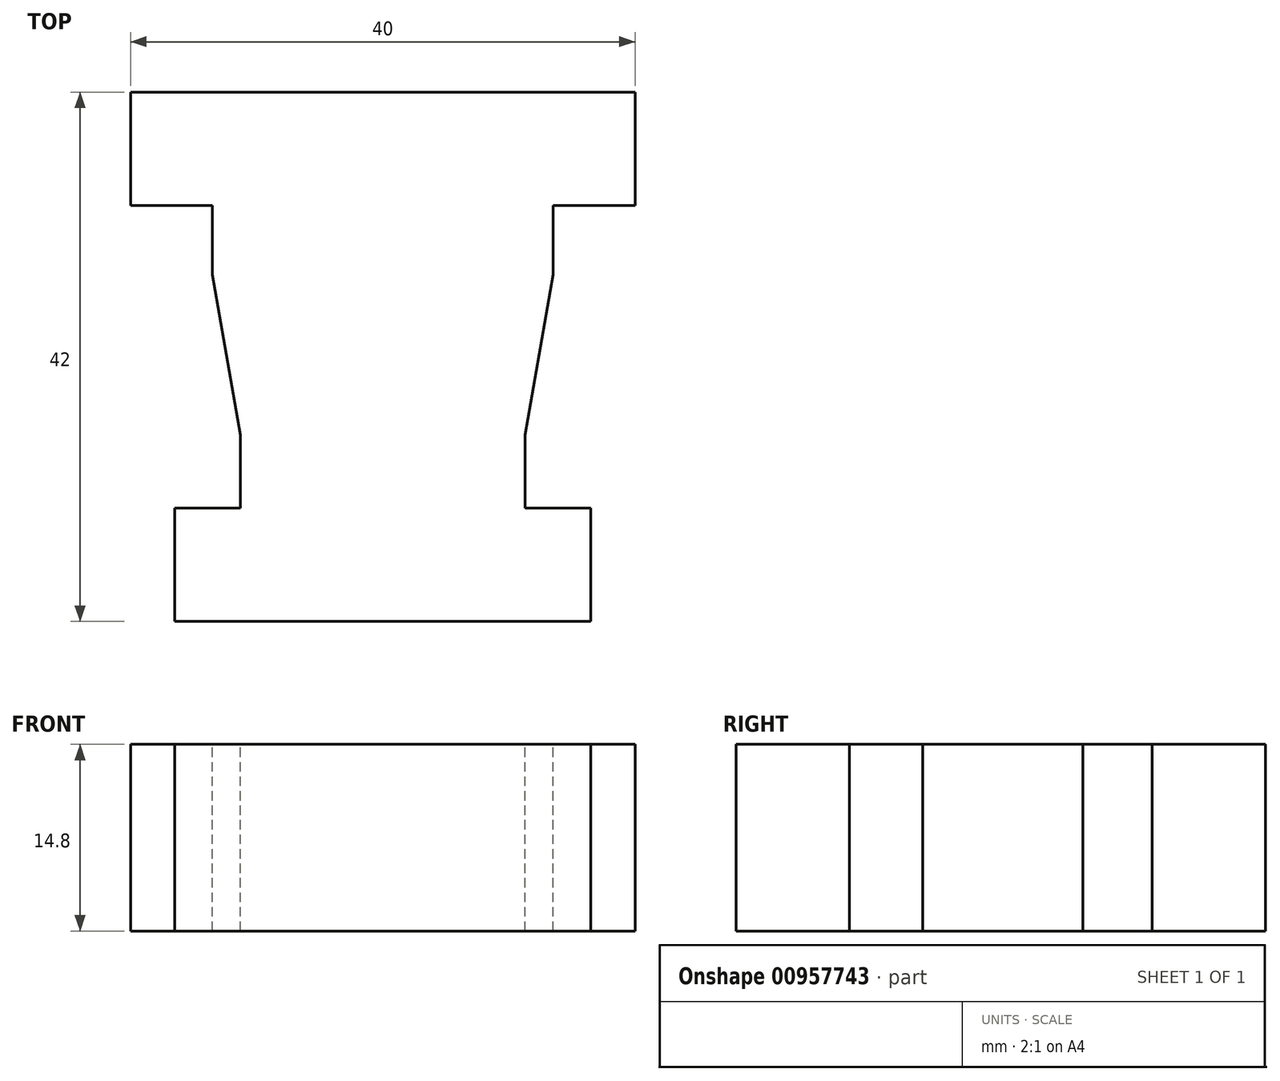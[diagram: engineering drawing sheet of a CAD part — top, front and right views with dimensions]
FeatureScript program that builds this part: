
annotation { "Feature Type Name" : "Feature", "Feature Type Description" : "" }
export const myFeature = defineFeature(function(context is Context, id is Id, definition is map)
    precondition{}
    {
        {
            var Q0;
            Q0=qCreatedBy(makeId("Top.planeOp"),FACE);
            var sketch = newSketch(context, id + "F0", { "sketchPlane" : qUnion([Q0])});
            skLineSegment(sketch, "E0.bottom", {"start": v(20, 21) * mm, "end": v(-20, 21) * mm});
            skLineSegment(sketch, "E0.top", {"start": v(20, -21) * mm, "end": v(-20, -21) * mm});
            skLineSegment(sketch, "E0.left", {"start": v(20, 21) * mm, "end": v(20, -21) * mm});
            skLineSegment(sketch, "E0.right", {"start": v(-20, 21) * mm, "end": v(-20, -21) * mm});
            skPoint(sketch, "E0.middle", {"position": v(0, 0) * mm});
            skSolve(sketch);
        }
        {
            var Q0;
            Q0=makeQuery(id+"F0.imprint","IMPRINT",FACE,{"disambiguationData":[TD([[makeQuery(id+"F0.imprint","IMPRINT",EDGE,{"derivedFrom":sQuery(id+"F0.wireOp",EDGE,"E0.bottom")}),1.0]])]});
            extrude(context, id + "F1", {"entities" : qUnion([Q0]), "depth" : 14.8 * mm, "offsetDistance" : 25 * mm});
        }
        {
            var Q0;
            Q0=makeQuery(id+"F1.opExtrude","CAP_FACE",FACE,{"disambiguationData":[OSD([sQuery(id+"F0.wireOp",EDGE,"E0.bottom"),sQuery(id+"F0.wireOp",EDGE,"E0.top"),sQuery(id+"F0.wireOp",EDGE,"E0.left"),sQuery(id+"F0.wireOp",EDGE,"E0.right")])],"isStart":false});
            var sketch = newSketch(context, id + "F2", { "sketchPlane" : qUnion([Q0])});
            skLineSegment(sketch, "E1", {"start": v(-20, 12) * mm, "end": v(-13.5, 12) * mm});
            skLineSegment(sketch, "E2", {"start": v(-13.5, 12) * mm, "end": v(-13.5, 6.5) * mm});
            skLineSegment(sketch, "E3", {"start": v(-13.5, 6.5) * mm, "end": v(-11.3, -6.2) * mm});
            skLineSegment(sketch, "E4", {"start": v(-11.3, -6.2) * mm, "end": v(-11.3, -12) * mm});
            skLineSegment(sketch, "E5", {"start": v(-11.3, -12) * mm, "end": v(-16.5, -12) * mm});
            skLineSegment(sketch, "E6", {"start": v(-16.5, -12) * mm, "end": v(-16.5, -21) * mm});
            skLineSegment(sketch, "E7", {"start": v(-16.5, -21) * mm, "end": v(-20, -21) * mm});
            skLineSegment(sketch, "E8", {"start": v(-20, -21) * mm, "end": v(-20, 12) * mm});
            skLineSegment(sketch, "E9", {"start": v(0, 0) * mm, "end": v(0, 21) * mm, "construction": true});
            skLineSegment(sketch, "E10.MirrorCS", {"start": v(13.5, 6.5) * mm, "end": v(11.3, -6.2) * mm});
            skLineSegment(sketch, "E11.MirrorCS", {"start": v(13.5, 12) * mm, "end": v(13.5, 6.5) * mm});
            skLineSegment(sketch, "E12.MirrorCS", {"start": v(20, 12) * mm, "end": v(13.5, 12) * mm});
            skLineSegment(sketch, "E13.MirrorCS", {"start": v(20, -21) * mm, "end": v(20, 12) * mm});
            skLineSegment(sketch, "E14.MirrorCS", {"start": v(16.5, -21) * mm, "end": v(20, -21) * mm});
            skLineSegment(sketch, "E15.MirrorCS", {"start": v(16.5, -12) * mm, "end": v(16.5, -21) * mm});
            skLineSegment(sketch, "E16.MirrorCS", {"start": v(11.3, -12) * mm, "end": v(16.5, -12) * mm});
            skLineSegment(sketch, "E17.MirrorCS", {"start": v(11.3, -6.2) * mm, "end": v(11.3, -12) * mm});
            skSolve(sketch);
        }
        {
            var Q0;
            Q0=makeQuery(id+"F2.imprint","IMPRINT",FACE,{"disambiguationData":[TD([[makeQuery(id+"F2.imprint","IMPRINT",EDGE,{"derivedFrom":sQuery(id+"F2.wireOp",EDGE,"E1")}),-1.0]])]});
            var Q1;
            Q1=makeQuery(id+"F2.imprint","IMPRINT",FACE,{"disambiguationData":[TD([[makeQuery(id+"F2.imprint","IMPRINT",EDGE,{"derivedFrom":sQuery(id+"F2.wireOp",EDGE,"E10.MirrorCS")}),1.0]])]});
            extrude(context, id + "F3", {"entities" : qUnion([Q0, Q1]), "operationType" : NewBodyOperationType.REMOVE, "oppositeDirection" : true, "depth" : 25 * mm, "offsetDistance" : 25 * mm});
        }
    });
